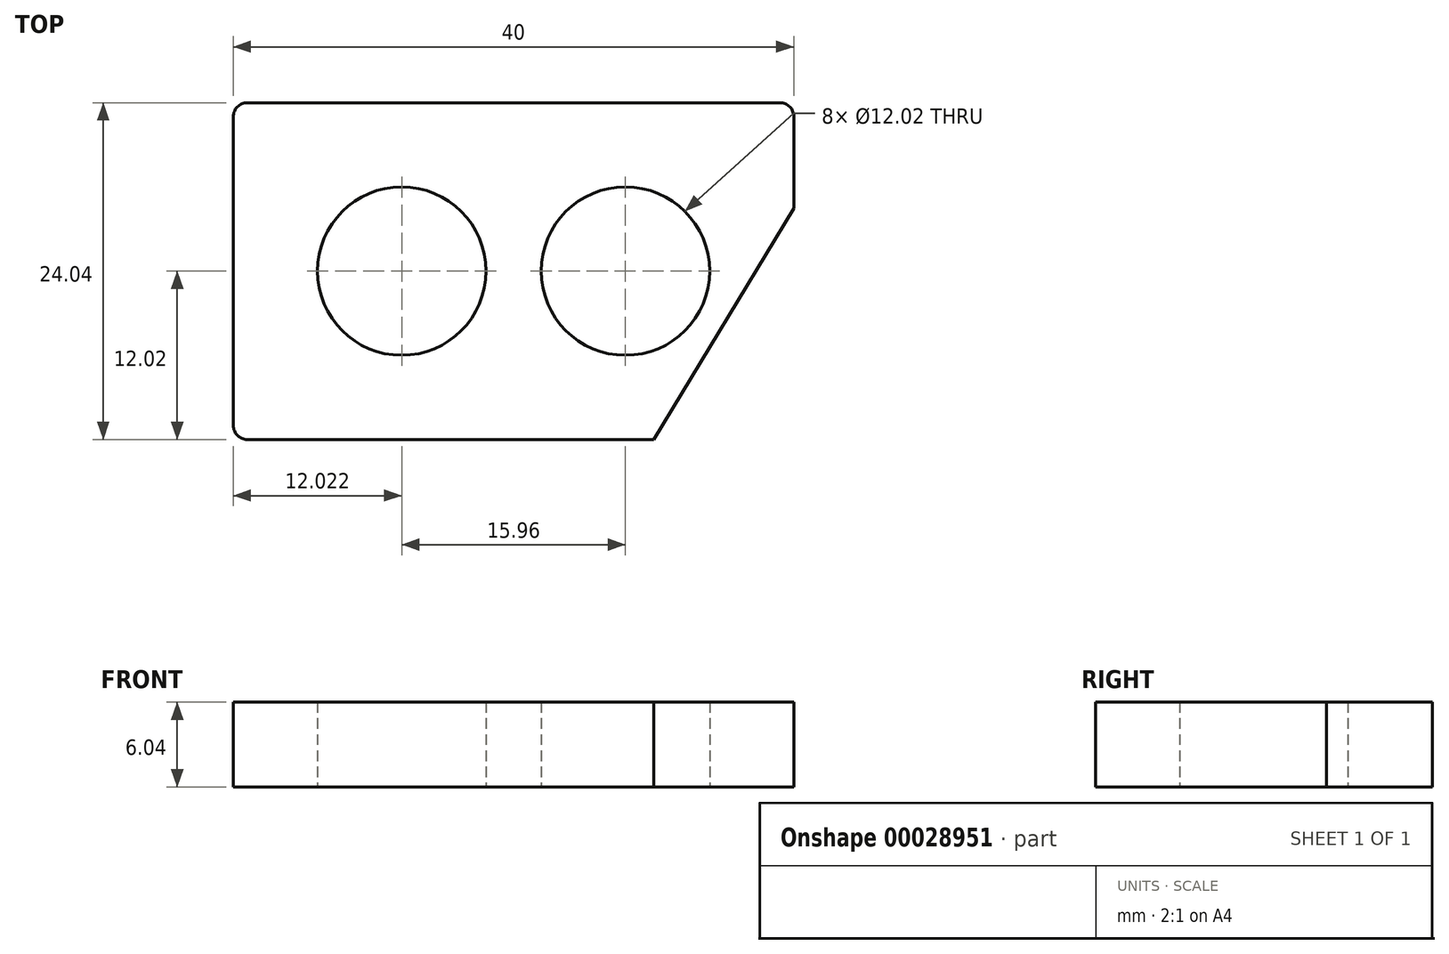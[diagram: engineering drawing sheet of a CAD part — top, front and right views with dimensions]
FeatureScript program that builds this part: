
annotation { "Feature Type Name" : "Feature", "Feature Type Description" : "" }
export const myFeature = defineFeature(function(context is Context, id is Id, definition is map)
    precondition{}
    {
        {
            var Q0;
            Q0=qCreatedBy(makeId("Top.planeOp"),FACE);
            var sketch = newSketch(context, id + "F0", { "sketchPlane" : qUnion([Q0])});
            skLineSegment(sketch, "E0.bottom", {"start": v(-43.42, 12.02) * mm, "end": v(-5.42, 12.02) * mm});
            skLineSegment(sketch, "E0.top", {"start": v(-43.42, -12.02) * mm, "end": v(-14.42, -12.02) * mm});
            skLineSegment(sketch, "E0.left", {"start": v(-44.42, 11.02) * mm, "end": v(-44.42, -11.02) * mm});
            skLineSegment(sketch, "E0.right", {"start": v(-4.42, 11.02) * mm, "end": v(-4.42, 4.48) * mm});
            skCircle(sketch, "E1", {"center": v(-32.4, 0) * mm, "radius": 6 * mm});
            skCircle(sketch, "E2", {"center": v(-16.44, 0) * mm, "radius": 6 * mm});
            skPoint(sketch, "E3.visualSharp", {"position": v(-44.42, -12.02) * mm});
            skArc(sketch, "E3.filletArc", {"start": v(-44.42, -11.02) * mm, "mid": v(-44.12, -11.73) * mm, "end": v(-43.42, -12.02) * mm});
            skPoint(sketch, "E4.visualSharp", {"position": v(-44.42, 12.02) * mm});
            skArc(sketch, "E4.filletArc", {"start": v(-43.42, 12.02) * mm, "mid": v(-44.12, 11.73) * mm, "end": v(-44.42, 11.02) * mm});
            skPoint(sketch, "E5.visualSharp", {"position": v(-4.42, -12.02) * mm});
            skPoint(sketch, "E6.visualSharp", {"position": v(-4.42, 12.02) * mm});
            skArc(sketch, "E6.filletArc", {"start": v(-4.42, 11.02) * mm, "mid": v(-4.71, 11.73) * mm, "end": v(-5.42, 12.02) * mm});
            skLineSegment(sketch, "E7", {"start": v(-14.42, -12.02) * mm, "end": v(-4.42, 4.48) * mm});
            skSolve(sketch);
        }
        {
            var Q0;
            Q0=makeQuery(id+"F0.imprint","IMPRINT",FACE,{"disambiguationData":[TD([[makeQuery(id+"F0.imprint","IMPRINT",EDGE,{"derivedFrom":sQuery(id+"F0.wireOp",EDGE,"E0.bottom")}),-1.0]])]});
            extrude(context, id + "F1", {"entities" : qUnion([Q0]), "depth" : 6.04 * mm});
        }
    });
